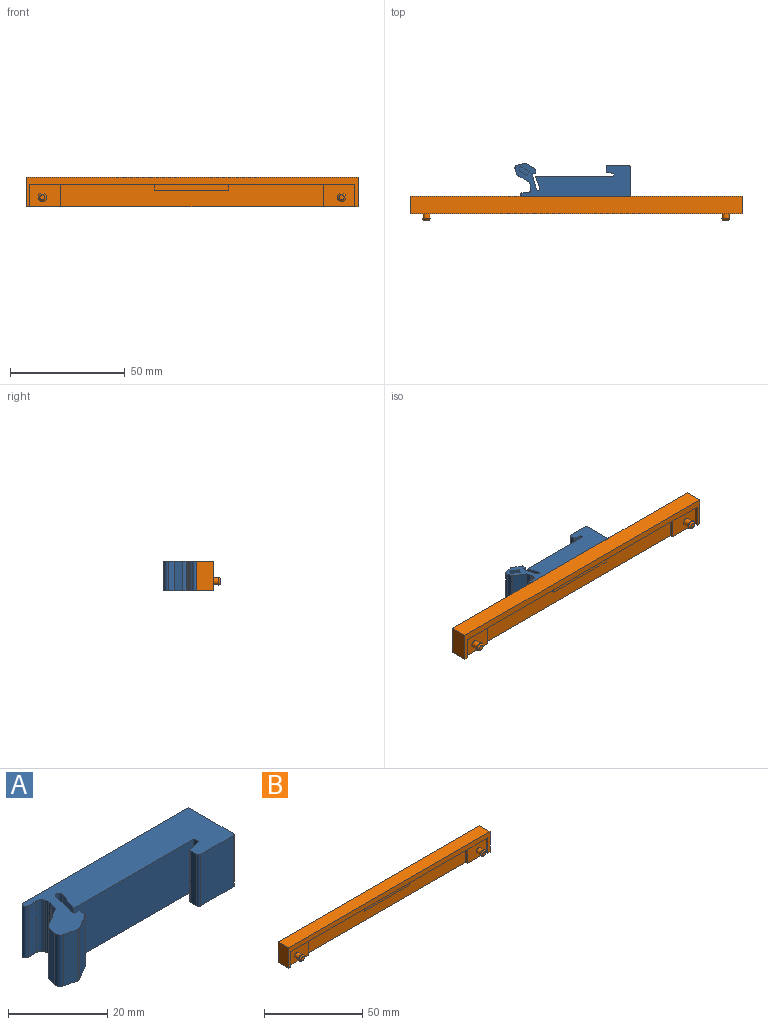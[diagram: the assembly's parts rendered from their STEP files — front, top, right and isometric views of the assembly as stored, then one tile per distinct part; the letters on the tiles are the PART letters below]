
ASSEMBLY  parts=2 mates=1
PART A: 40 faces, bbox 50.2x14.3x12.7 mm
  f0: plane 10.16x0.71mm, normal (-0.59,0.81,0), area 8.9mm2, adj f1,f4,f38,f39
  f1: plane 10.16x2.94mm, normal (-0.51,0.86,0), area 34.7mm2, adj f0,f2,f38,f39
  f2: plane 10.16x1.71mm, normal (0.86,0.51,0), area 20.1mm2, adj f1,f3,f38,f39
  f3: plane 10.16x3.67mm, normal (0.51,-0.86,0), area 43.3mm2, adj f2,f4,f38,f39
  f4: plane 10.16x1.62mm, normal (-0.85,-0.52,0), area 19.3mm2, adj f0,f3,f38,f39
  f5: plane 47.12x12.7mm, normal (0,1,0), area 598.5mm2, adj f6,f36,f37,f38
  f6: cylinder r=0.74mm len=12.7mm, axis (0,0,-1), area 29.6mm2, adj f5,f7,f37,f38
  f7: plane 12.7x2.48mm, normal (0,-1,0), area 31.4mm2, adj f6,f8,f37,f38
  f8: cylinder r=1.18mm len=12.7mm, axis (0,0,-1), area 21.4mm2, adj f7,f9,f37,f38
  f9: plane 12.7x0.48mm, normal (-0.98,-0.22,0), area 6.2mm2, adj f8,f10,f37,f38
  f10: plane 12.7x0.49mm, normal (-1,-0.07,0), area 6.2mm2, adj f9,f11,f37,f38
  f11: plane 12.7x0.48mm, normal (-1,0.07,0), area 6.2mm2, adj f10,f12,f37,f38
  f12: plane 12.7x0.49mm, normal (-0.98,0.22,0), area 6.3mm2, adj f11,f13,f37,f38
  f13: plane 12.7x1.73mm, normal (-0.96,0.29,0), area 23mm2, adj f12,f14,f37,f38
  f14: plane 12.7x5.43mm, normal (-0.52,0.85,0), area 80.7mm2, adj f13,f15,f37,f38
  f15: cylinder r=0.52mm len=12.7mm, axis (0,0,-1), area 5.2mm2, adj f14,f16,f37,f38
  f16: plane 12.7x2.32mm, normal (-0.97,0.23,0), area 30.3mm2, adj f15,f17,f37,f38
  f17: cylinder r=1.3mm len=12.7mm, axis (0,0,-1), area 25.9mm2, adj f16,f18,f37,f38
  f18: plane 12.7x3.18mm, normal (-0.23,-0.97,0), area 41.4mm2, adj f17,f19,f37,f38
  f19: cylinder r=1.26mm len=12.7mm, axis (0,0,-1), area 10.8mm2, adj f18,f20,f37,f38
  f20: plane 12.7x4.02mm, normal (0.51,-0.86,0), area 59.2mm2, adj f19,f21,f37,f38
  f21: cylinder r=0.26mm len=12.7mm, axis (0,0,-1), area 2.2mm2, adj f20,f22,f37,f38
  f22: plane 12.7x1.71mm, normal (1,0,0), area 21.7mm2, adj f21,f23,f37,f38
  f23: plane 12.7x1.3mm, normal (0,1,0), area 16.5mm2, adj f22,f24,f37,f38
  f24: plane 12.7x1.2mm, normal (1,0,0), area 15.2mm2, adj f23,f25,f37,f38
  f25: plane 12.7x5.64mm, normal (0.96,-0.26,0), area 74.3mm2, adj f24,f26,f37,f38
  f26: cylinder r=0.75mm len=12.7mm, axis (0,0,-1), area 30mm2, adj f25,f27,f37,f38
  f27: plane 12.7x5.03mm, normal (-0.94,0.34,0), area 68mm2, adj f26,f28,f37,f38
  f28: plane 34.28x12.7mm, normal (0,-1,0), area 435.4mm2, adj f27,f29,f37,f38
  f29: plane 12.7x1.21mm, normal (-1,0,0), area 15.4mm2, adj f28,f30,f37,f38
  f30: plane 12.7x3.02mm, normal (-0.21,0.98,0), area 39.2mm2, adj f29,f31,f37,f38
  f31: cylinder r=0.52mm len=12.7mm, axis (0,0,-1), area 8.2mm2, adj f30,f32,f37,f38
  f32: plane 12.7x1.84mm, normal (-1,0,0), area 23.3mm2, adj f31,f33,f37,f38
  f33: cylinder r=0.52mm len=12.7mm, axis (0,0,-1), area 10.4mm2, adj f32,f34,f37,f38
  f34: plane 12.7x9.33mm, normal (0,-1,0), area 118.5mm2, adj f33,f35,f37,f38
  f35: cylinder r=0.52mm len=12.7mm, axis (0,0,-1), area 10.3mm2, adj f34,f36,f37,f38
  f36: plane 12.83x12.7mm, normal (1,0,0), area 162.9mm2, adj f5,f35,f37,f38
  f37: plane 50.17x14.34mm, normal (0,0,1), area 464mm2, adj f5,f6,f7,f8,f9,f10,f11,f12
  f38: plane 50.17x14.34mm, normal (0,0,-1), area 455.6mm2, adj f0,f1,f2,f3,f4,f5,f6,f7
  f39: plane 4.66x3.87mm, normal (0,0,-1), area 8.4mm2, adj f0,f1,f2,f3,f4
PART B: 28 faces, bbox 144.8x10.6x12.7 mm
  f0: plane 144.78x12.7mm, normal (0,-1,0), area 472.7mm2, adj f1,f3,f4,f5,f6,f8,f9
  f1: plane 12.7x7.62mm, normal (1,0,0), area 96.8mm2, adj f0,f2,f4,f5
  f2: plane 144.78x12.7mm, normal (0,1,0), area 1838.7mm2, adj f1,f3,f4,f5
  f3: plane 12.7x7.62mm, normal (-1,0,0), area 96.8mm2, adj f0,f2,f4,f5
  f4: plane 144.78x7.62mm, normal (0,0,1), area 1103.2mm2, adj f0,f1,f2,f3
  f5: plane 144.78x7.62mm, normal (0,0,-1), area 778.1mm2, adj f0,f1,f2,f3,f6,f7,f8,f10
  f6: plane 9.64x1.27mm, normal (1,0,0), area 12.2mm2, adj f0,f5,f7,f9
  f7: plane 13.7x9.64mm, normal (0,-1,0), area 125mm2, adj f5,f6,f9,f13,f18
  f8: plane 9.64x1.27mm, normal (-1,0,0), area 12.2mm2, adj f0,f5,f9,f10
  f9: plane 141.7x2.54mm, normal (0,0,-1), area 283.8mm2, adj f0,f6,f7,f8,f10,f11,f12,f13
  f10: plane 13.7x9.64mm, normal (0,-1,0), area 125mm2, adj f5,f8,f9,f14,f19
  f11: plane 32.51x2.54mm, normal (0,-1,0), area 82.6mm2, adj f9,f12,f15,f16
  f12: plane 2.54x1.27mm, normal (-1,0,0), area 3.2mm2, adj f9,f11,f16,f17
  f13: plane 9.64x1.27mm, normal (1,0,0), area 12.2mm2, adj f5,f7,f9,f17
  f14: plane 9.64x1.27mm, normal (-1,0,0), area 12.2mm2, adj f5,f9,f10,f17
  f15: plane 2.54x1.27mm, normal (1,0,0), area 3.2mm2, adj f9,f11,f16,f17
  f16: plane 32.51x1.27mm, normal (0,0,-1), area 41.3mm2, adj f11,f12,f15,f17
  f17: plane 114.3x9.64mm, normal (0,-1,0), area 1019.3mm2, adj f5,f9,f12,f13,f14,f15,f16
  f18: cylinder r=1.5mm len=3.27mm, axis (0,1,0), area 30.8mm2, adj f7,f22
  f19: cylinder r=1.5mm len=3.27mm, axis (0,1,0), area 30.8mm2, adj f10,f25
  f20: cylinder r=1.85mm len=3.7mm, axis (0,1,0), area 2.8mm2, adj f22,f27
  f21: plane 2.18x2.18mm, normal (0,-1,0), area 3.7mm2, adj f27
  f22: plane 3.7x3.7mm, normal (0,1,0), area 3.7mm2, adj f18,f20
  f23: cylinder r=1.85mm len=3.7mm, axis (0,1,0), area 2.8mm2, adj f25,f26
  f24: plane 2.18x2.18mm, normal (0,-1,0), area 3.7mm2, adj f26
  f25: plane 3.7x3.7mm, normal (0,1,0), area 3.7mm2, adj f19,f23
  f26: cone r=1.09mm half-angle=45deg, axis (0,1,0), area 9.9mm2, adj f23,f24
  f27: cone r=1.09mm half-angle=45deg, axis (0,1,0), area 9.9mm2, adj f20,f21
PLACE A rot(axis=(1,0,0),180deg) t=(-1.43,22.45,12.7)mm
PLACE B at identity fixed
MATE fastened B.f2 <-> A.f5  axis (0,1,0) through (0.07,15.13,6.35)mm
